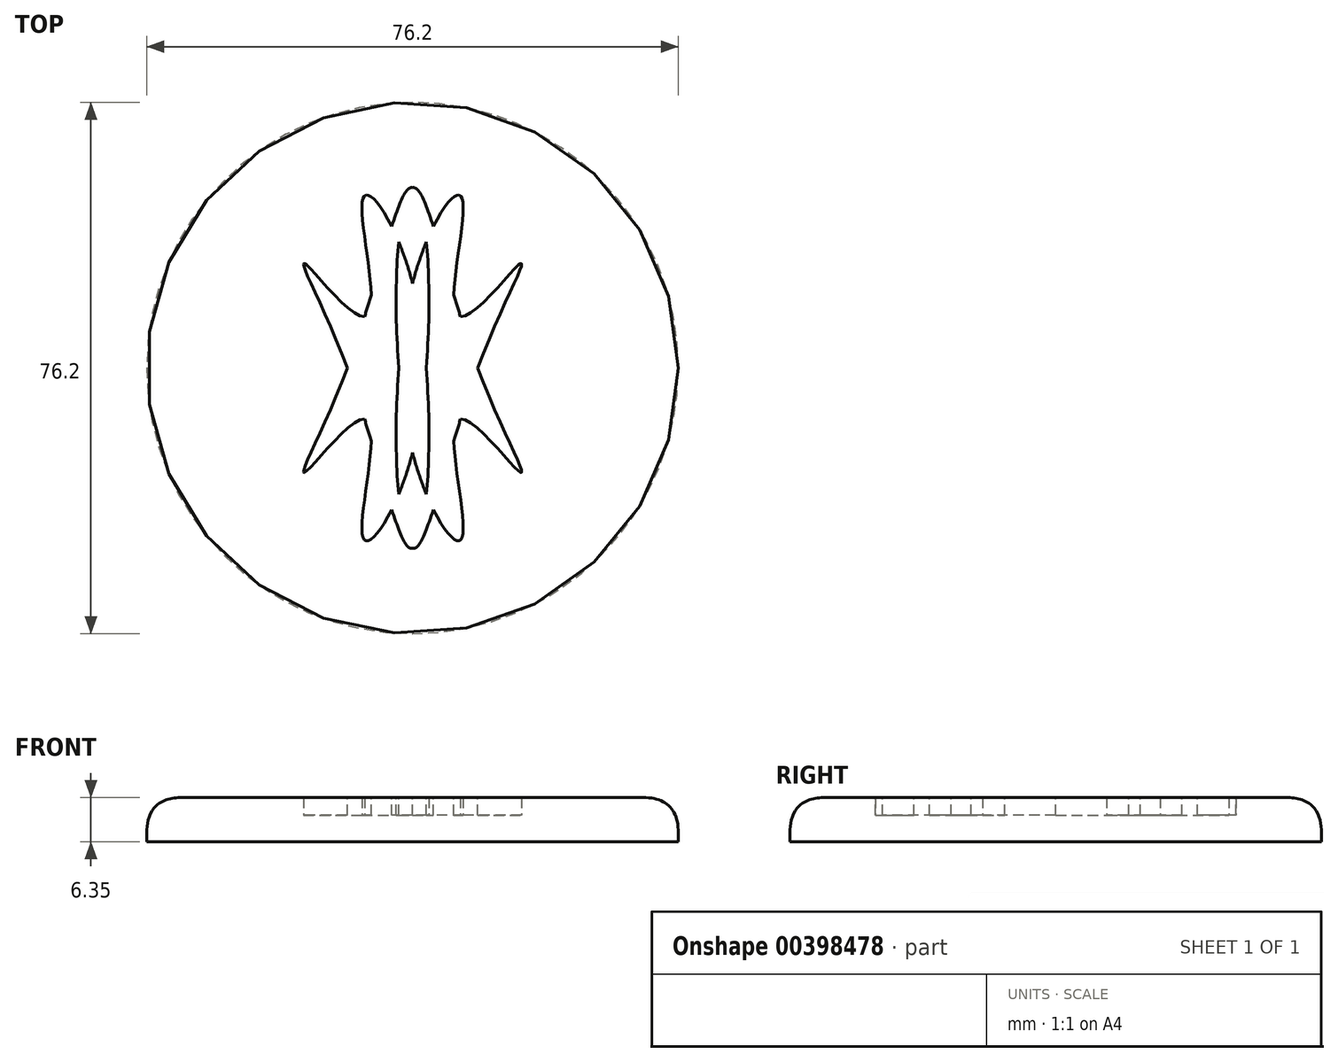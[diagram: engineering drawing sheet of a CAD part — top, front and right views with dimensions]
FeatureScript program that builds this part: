
annotation { "Feature Type Name" : "Feature", "Feature Type Description" : "" }
export const myFeature = defineFeature(function(context is Context, id is Id, definition is map)
    precondition{}
    {
        {
            var Q0;
            Q0=qCreatedBy(makeId("Top.planeOp"),FACE);
            var sketch = newSketch(context, id + "F0", { "sketchPlane" : qUnion([Q0])});
            skCircle(sketch, "E0", {"center": v(0, 0) * mm, "radius": 38.1 * mm});
            skSolve(sketch);
        }
        {
            var Q0;
            Q0=makeQuery(id+"F0.imprint","IMPRINT",FACE,{"disambiguationData":[TD([[makeQuery(id+"F0.imprint","IMPRINT",EDGE,{"derivedFrom":sQuery(id+"F0.wireOp",EDGE,"E0")}),1.0]])]});
            extrude(context, id + "F1", {"entities" : qUnion([Q0]), "depth" : 6.35 * mm});
        }
        {
            var Q0;
            Q0=makeQuery(id+"F1.opExtrude","CAP_EDGE",EDGE,{"disambiguationData":[OSD([sQuery(id+"F0.wireOp",EDGE,"E0")])],"isStart":false});
            fillet(context, id + "F2", {"entities" : qUnion([Q0]), "radius" : 5.08 * mm, "tangentPropagation" : true, "rho" : 0.5, "crossSection" : FilletCrossSection.CONIC, "allowEdgeOverflow" : false});
        }
        {
            var Q0;
            Q0=makeQuery(id+"F1.opExtrude","CAP_FACE",FACE,{"disambiguationData":[OSD([sQuery(id+"F0.wireOp",EDGE,"E0")])],"isStart":false});
            var sketch = newSketch(context, id + "F3", { "sketchPlane" : qUnion([Q0])});
            skSolve(sketch);
        }
        {
            var Q0;
            {var subQ0=sQuery(id+"F0.wireOp",EDGE,"E0");Q0=makeQuery(id+"F3.imprint","IMPRINT",FACE,{"disambiguationData":[TD([[makeQuery(id+"F3.imprint","IMPRINT",EDGE,{"derivedFrom":makeQuery(id+"F2.opFillet","BLEND_EDGE",EDGE,{"blendedFrom":[makeQuery(id+"F1.opExtrude","CAP_EDGE",EDGE,{"disambiguationData":[OSD([subQ0])],"isStart":false}),makeQuery(id+"F1.opExtrude","CAP_FACE",FACE,{"disambiguationData":[OSD([subQ0])],"isStart":false})],"blendedInto":[makeQuery(id+"F1.opExtrude","CAP_FACE",FACE,{"disambiguationData":[OSD([subQ0])],"isStart":false})]})}),1.0]])]});}
            var sketch = newSketch(context, id + "F4", { "sketchPlane" : qUnion([Q0])});
            skFitSpline(sketch, "E1.MirrorC", {"points": [v(0, 25.85) * mm, v(-9.35, 0) * mm, v(-15.29, -14.86) * mm, v(-6.64, -7.4) * mm, v(-7.15, -24.19) * mm, v(0, -12.14) * mm, v(0, 25.85) * mm]});
            skFitSpline(sketch, "E2.MirrorC", {"points": [v(0, 25.85) * mm, v(9.35, 0) * mm, v(15.29, -14.86) * mm, v(6.64, -7.4) * mm, v(7.15, -24.19) * mm, v(0, -12.14) * mm, v(0, 25.85) * mm]});
            skFitSpline(sketch, "E3.trimOffspring", {"points": [v(0, -25.85) * mm, v(-9.35, 0) * mm, v(-15.29, 14.86) * mm, v(-6.64, 7.4) * mm, v(-7.15, 24.19) * mm, v(0, 12.14) * mm, v(0, -25.85) * mm]});
            skFitSpline(sketch, "E4.trimOffspring", {"points": [v(0, -25.85) * mm, v(9.35, 0) * mm, v(15.29, 14.86) * mm, v(6.64, 7.4) * mm, v(7.15, 24.19) * mm, v(0, 12.14) * mm, v(0, -25.85) * mm]});
            skCircle(sketch, "E5", {"center": v(0, 6.48) * mm, "radius": 2.2 * mm});
            skCircle(sketch, "E6.MirrorC", {"center": v(0, -6.48) * mm, "radius": 2.2 * mm});
            skSolve(sketch);
        }
        {
            var Q0;
            Q0 = qSketchRegion(id + "F4", true);
            extrude(context, id + "F5", {"entities" : qUnion([Q0]), "operationType" : NewBodyOperationType.REMOVE, "oppositeDirection" : true, "depth" : 2.54 * mm});
        }
    });
